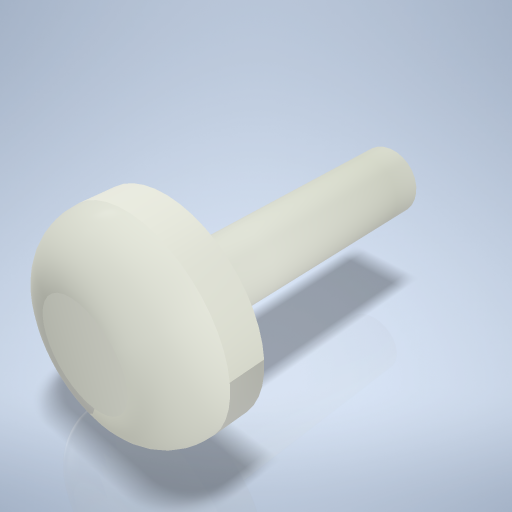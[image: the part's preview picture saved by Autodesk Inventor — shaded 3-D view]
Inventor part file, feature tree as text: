
AUTODESK INVENTOR PART (.ipt)
format: ipt  version: 2024.2 (Build 282272000, 272)  size: 270,336 bytes
history: native  units: mm
features: extrude x2, sketch x2, fillet x1
ambient origin geometry x8: Origin, YZ Plane, XZ Plane, XY Plane, X Axis, Y Axis, Z Axis, Center Point
bodies: Volumenkörper1 (feature_tree)
feature tree (5):
  extrude  "Extrusion1"  Depth=2.5mm TaperAngle=0.0deg
  extrude  "Extrusion2"  Depth=8.0mm TaperAngle=0.0deg
  fillet  "Rundung1"  Radius=1.5mm
  sketch  "Skizze1"  dims[d0=6.0mm d1=2.5mm d2=0.0mm]
  sketch  "Skizze2"  dims[d3=2.0mm d4=8.0mm d5=0.0mm d6=1.5mm]
